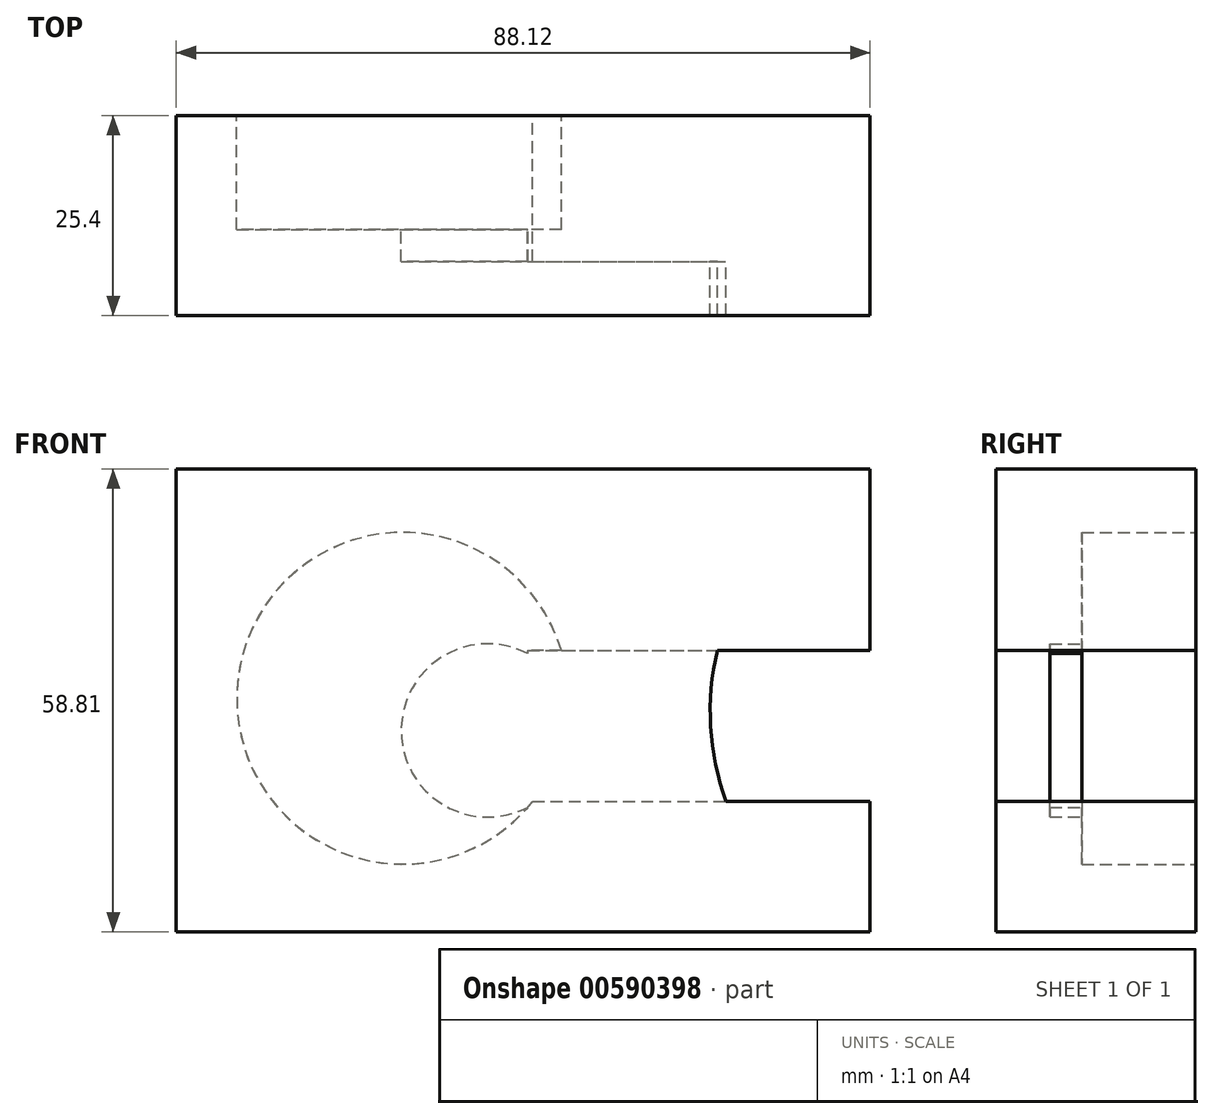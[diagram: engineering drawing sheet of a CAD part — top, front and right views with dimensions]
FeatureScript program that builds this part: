
annotation { "Feature Type Name" : "Feature", "Feature Type Description" : "" }
export const myFeature = defineFeature(function(context is Context, id is Id, definition is map)
    precondition{}
    {
        {
            var Q0;
            Q0=qCreatedBy(makeId("Front.planeOp"),FACE);
            var sketch = newSketch(context, id + "F0", { "sketchPlane" : qUnion([Q0])});
            skLineSegment(sketch, "E0.bottom", {"start": v(-36.6, 25.35) * mm, "end": v(51.53, 25.35) * mm});
            skLineSegment(sketch, "E0.top", {"start": v(-36.6, -33.46) * mm, "end": v(51.53, -33.46) * mm});
            skLineSegment(sketch, "E0.left", {"start": v(-36.6, 25.35) * mm, "end": v(-36.6, -33.46) * mm});
            skLineSegment(sketch, "E0.right", {"start": v(51.53, 25.35) * mm, "end": v(51.53, -33.46) * mm});
            skSolve(sketch);
        }
        {
            var Q0;
            Q0=makeQuery(id+"F0.imprint","IMPRINT",FACE,{"disambiguationData":[TD([[makeQuery(id+"F0.imprint","IMPRINT",EDGE,{"derivedFrom":sQuery(id+"F0.wireOp",EDGE,"E0.bottom")}),-1.0]])]});
            var sketch = newSketch(context, id + "F1", { "sketchPlane" : qUnion([Q0])});
            skCircle(sketch, "E1", {"center": v(-7.83, -3.78) * mm, "radius": 21.07 * mm});
            skLineSegment(sketch, "E2.bottom", {"start": v(8.02, 2.3) * mm, "end": v(56.5, 2.3) * mm});
            skLineSegment(sketch, "E2.top", {"start": v(8.02, -16.87) * mm, "end": v(56.5, -16.87) * mm});
            skLineSegment(sketch, "E2.left", {"start": v(8.02, 2.3) * mm, "end": v(8.02, -16.87) * mm});
            skLineSegment(sketch, "E2.right", {"start": v(56.5, 2.3) * mm, "end": v(56.5, -16.87) * mm});
            skSolve(sketch);
        }
        {
            var Q0;
            Q0=makeQuery(id+"F0.imprint","IMPRINT",FACE,{"disambiguationData":[TD([[makeQuery(id+"F0.imprint","IMPRINT",EDGE,{"derivedFrom":sQuery(id+"F0.wireOp",EDGE,"E0.bottom")}),-1.0]])]});
            extrude(context, id + "F2", {"entities" : qUnion([Q0]), "depth" : 25.4 * mm, "offsetDistance" : 25.4 * mm});
        }
        {
            var Q0;
            {var subQ5=sQuery(id+"F1.wireOp",EDGE,"E2.left");Q0=makeQuery(id+"F1.imprint","IMPRINT",FACE,{"disambiguationData":[TD([[makeQuery(id+"F1.imprint","IMPRINT",EDGE,{"derivedFrom":subQ5}),-1.0]])]});}
            var Q1;
            {var subQ0=sQuery(id+"F1.wireOp",EDGE,"E2.bottom");var subQ1=sQuery(id+"F1.wireOp",EDGE,"E1");var subQ2=makeQuery(id+"F1.imprint","INTERSECT",VERTEX,{"derivedFrom":[subQ1,subQ0]});Q1=makeQuery(id+"F1.imprint","IMPRINT",FACE,{"disambiguationData":[TD([[makeQuery(id+"F1.imprint","IMPRINT",EDGE,{"disambiguationData":[TD([[subQ2,1.0]])],"derivedFrom":subQ1}),-1.0]])]});}
            var Q2;
            {var subQ5=sQuery(id+"F1.wireOp",EDGE,"E2.left");Q2=makeQuery(id+"F1.imprint","IMPRINT",FACE,{"disambiguationData":[TD([[makeQuery(id+"F1.imprint","IMPRINT",EDGE,{"derivedFrom":subQ5}),1.0]])]});}
            extrude(context, id + "F3", {"entities" : qUnion([Q0, Q1, Q2]), "operationType" : NewBodyOperationType.REMOVE, "depth" : 14.48 * mm, "offsetDistance" : 25.4 * mm});
        }
        {
            var Q0;
            {var subQ5=sQuery(id+"F1.wireOp",EDGE,"E2.left");Q0=makeQuery(id+"F1.imprint","IMPRINT",FACE,{"disambiguationData":[TD([[makeQuery(id+"F1.imprint","IMPRINT",EDGE,{"derivedFrom":subQ5}),-1.0]])]});}
            var sketch = newSketch(context, id + "F4", { "sketchPlane" : qUnion([Q0])});
            skCircle(sketch, "E3", {"center": v(2.97, -7.86) * mm, "radius": 11 * mm});
            skSolve(sketch);
        }
        {
            var Q0;
            {var subQ2=sQuery(id+"F1.wireOp",EDGE,"E2.top");var subQ6=sQuery(id+"F1.wireOp",EDGE,"E2.left");var subQ9=makeQuery(id+"F1.imprint","IMPRINT",EDGE,{"disambiguationData":[TD([[makeQuery(id+"F1.imprint","INTERSECT",VERTEX,{"derivedFrom":[subQ2,subQ6]}),-1.0]])],"derivedFrom":subQ2});Q0=makeQuery(id+"F4.imprint","IMPRINT",FACE,{"disambiguationData":[TD([[makeQuery(id+"F4.imprint","IMPRINT",EDGE,{"derivedFrom":subQ9}),-1.0]])]});}
            var Q1;
            {var subQ0=sQuery(id+"F1.wireOp",EDGE,"E2.bottom");var subQ1=sQuery(id+"F1.wireOp",EDGE,"E1");var subQ2=makeQuery(id+"F1.imprint","INTERSECT",VERTEX,{"derivedFrom":[subQ1,subQ0]});Q1=makeQuery(id+"F1.imprint","IMPRINT",FACE,{"disambiguationData":[TD([[makeQuery(id+"F1.imprint","IMPRINT",EDGE,{"disambiguationData":[TD([[subQ2,1.0]])],"derivedFrom":subQ1}),-1.0]])]});}
            var Q2;
            {var subQ5=sQuery(id+"F1.wireOp",EDGE,"E2.left");Q2=makeQuery(id+"F1.imprint","IMPRINT",FACE,{"disambiguationData":[TD([[makeQuery(id+"F1.imprint","IMPRINT",EDGE,{"derivedFrom":subQ5}),1.0]])]});}
            extrude(context, id + "F5", {"entities" : qUnion([Q0, Q1, Q2]), "operationType" : NewBodyOperationType.REMOVE, "depth" : 18.54 * mm, "offsetDistance" : 25.4 * mm});
        }
        {
            var Q0;
            {var subQ9=makeQuery(id+"F0.imprint","IMPRINT",EDGE,{"derivedFrom":sQuery(id+"F0.wireOp",EDGE,"E0.bottom")});Q0=makeQuery(id+"F1.imprint","IMPRINT",FACE,{"disambiguationData":[TD([[makeQuery(id+"F1.imprint","IMPRINT",EDGE,{"derivedFrom":subQ9}),-1.0]])]});}
            var sketch = newSketch(context, id + "F6", { "sketchPlane" : qUnion([Q0])});
            skCircle(sketch, "E4", {"center": v(64.43, -5.44) * mm, "radius": 33.2 * mm});
            skSolve(sketch);
        }
        {
            var Q0;
            {var subQ0=makeQuery(id+"F0.imprint","IMPRINT",EDGE,{"derivedFrom":sQuery(id+"F0.wireOp",EDGE,"E0.right")});var subQ9=makeQuery(id+"F0.imprint","IMPRINT",EDGE,{"derivedFrom":sQuery(id+"F0.wireOp",EDGE,"E0.top")});var subQ12=makeQuery(id+"F1.imprint","IMPRINT",EDGE,{"disambiguationData":[TD([[makeQuery(id+"F1.imprint","INTERSECT",VERTEX,{"derivedFrom":[subQ9,subQ0]}),1.0]])],"derivedFrom":subQ0});Q0=makeQuery(id+"F6.imprint","IMPRINT",FACE,{"disambiguationData":[TD([[makeQuery(id+"F6.imprint","IMPRINT",EDGE,{"derivedFrom":subQ12}),1.0]])]});}
            extrude(context, id + "F7", {"entities" : qUnion([Q0]), "operationType" : NewBodyOperationType.REMOVE, "depth" : 31.5 * mm, "offsetDistance" : 25.4 * mm});
        }
        {
            var Q0;
            {var subQ0=makeQuery(id+"F0.imprint","IMPRINT",EDGE,{"derivedFrom":sQuery(id+"F0.wireOp",EDGE,"E0.right")});var subQ9=makeQuery(id+"F0.imprint","IMPRINT",EDGE,{"derivedFrom":sQuery(id+"F0.wireOp",EDGE,"E0.top")});var subQ12=makeQuery(id+"F1.imprint","IMPRINT",EDGE,{"disambiguationData":[TD([[makeQuery(id+"F1.imprint","INTERSECT",VERTEX,{"derivedFrom":[subQ9,subQ0]}),1.0]])],"derivedFrom":subQ0});Q0=makeQuery(id+"F6.imprint","IMPRINT",FACE,{"disambiguationData":[TD([[makeQuery(id+"F6.imprint","IMPRINT",EDGE,{"derivedFrom":subQ12}),1.0]])]});}
            extrude(context, id + "F8", {"entities" : qUnion([Q0]), "operationType" : NewBodyOperationType.REMOVE, "depth" : 32 * mm, "offsetDistance" : 25.4 * mm});
        }
    });
